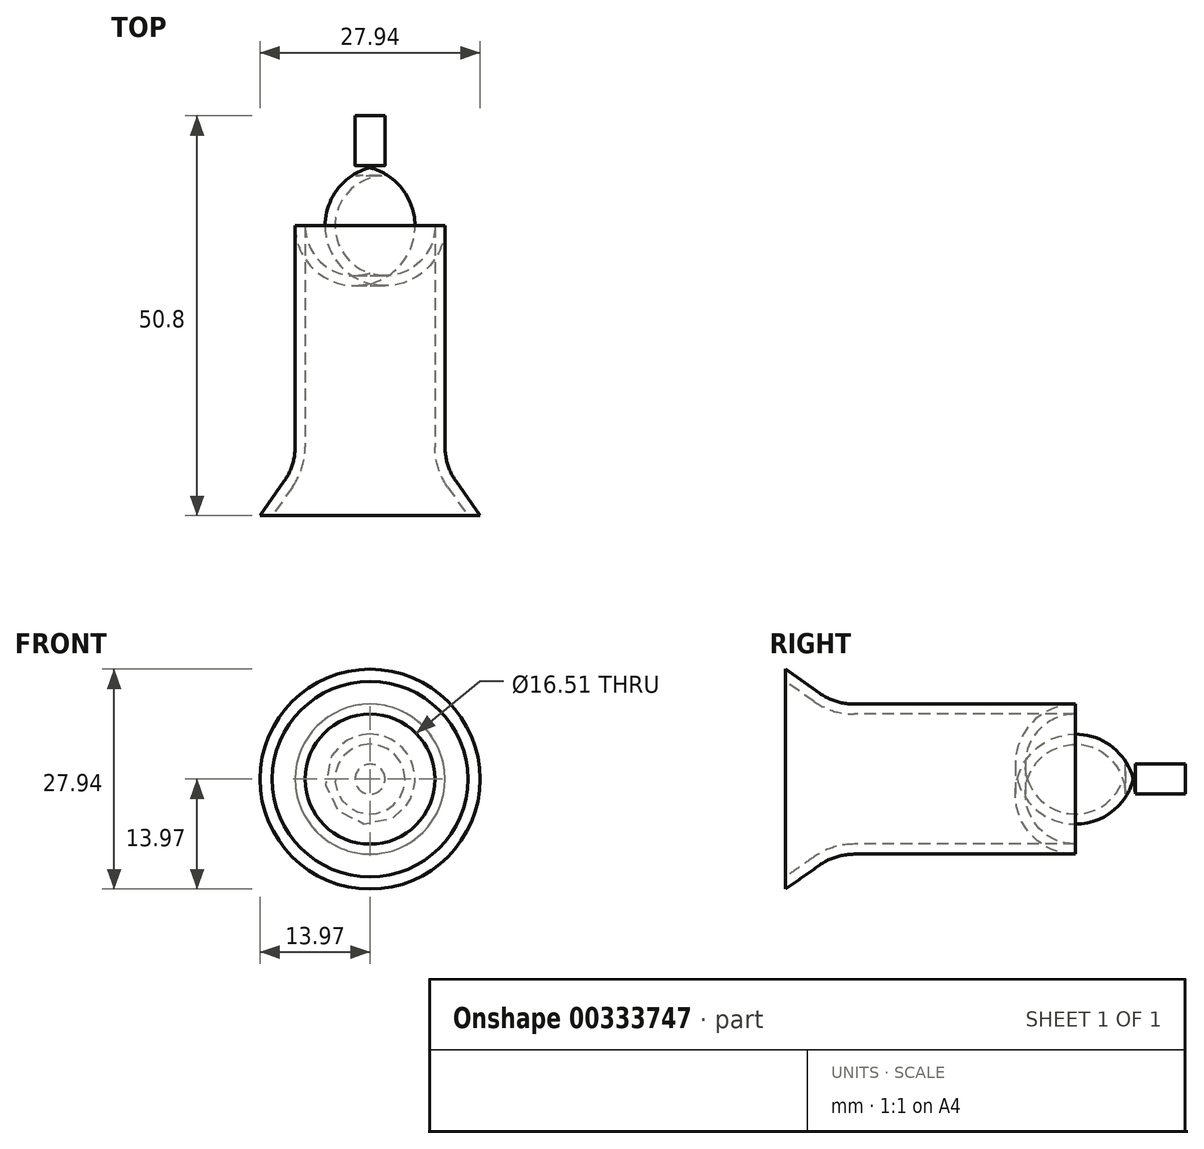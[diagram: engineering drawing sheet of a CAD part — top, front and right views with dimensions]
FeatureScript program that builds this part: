
annotation { "Feature Type Name" : "Feature", "Feature Type Description" : "" }
export const myFeature = defineFeature(function(context is Context, id is Id, definition is map)
    precondition{}
    {
        {
            var Q0;
            Q0=qCreatedBy(makeId("Front.planeOp"),FACE);
            var sketch = newSketch(context, id + "F0", { "sketchPlane" : qUnion([Q0])});
            skCircle(sketch, "E0", {"center": v(0, 0) * mm, "radius": 13.97 * mm});
            skSolve(sketch);
        }
        {
            var Q0;
            Q0=qCreatedBy(makeId("Front.planeOp"),FACE);
            cPlane(context, id + "F1", {"entities" : qUnion([Q0]), "cplaneType" : CPlaneType.OFFSET, "offset" : 6.35 * mm, "oppositeDirection" : true, "width" : 152.4 * mm, "height" : 152.4 * mm});
        }
        {
            var Q0;
            Q0=qCreatedBy(id+"F1.planeOp",FACE);
            var sketch = newSketch(context, id + "F2", { "sketchPlane" : qUnion([Q0])});
            skCircle(sketch, "E1", {"center": v(0, 0) * mm, "radius": 9.53 * mm});
            skSolve(sketch);
        }
        {
            var Q0;
            Q0=makeQuery(id+"F0.imprint","IMPRINT",FACE,{"disambiguationData":[TD([[makeQuery(id+"F0.imprint","IMPRINT",EDGE,{"derivedFrom":sQuery(id+"F0.wireOp",EDGE,"E0")}),1.0]])]});
            var Q1;
            Q1=makeQuery(id+"F2.imprint","IMPRINT",FACE,{"disambiguationData":[TD([[makeQuery(id+"F2.imprint","IMPRINT",EDGE,{"derivedFrom":sQuery(id+"F2.wireOp",EDGE,"E1")}),1.0]])]});
            loft(context, id + "F3", {"sheetProfilesArray" : [{ "sheetProfileEntities" : qUnion([Q0]) }, { "sheetProfileEntities" : qUnion([Q1]) }]});
        }
        {
            var Q0;
            Q0 = qSketchRegion(id + "F2", true);
            extrude(context, id + "F4", {"entities" : qUnion([Q0]), "operationType" : NewBodyOperationType.ADD, "oppositeDirection" : true, "depth" : 38.1 * mm});
        }
        {
            var Q0;
            {var subQ0=sQuery(id+"F2.wireOp",EDGE,"E1");Q0=makeQuery(id+"F4.boolean.opBoolean","MERGE",EDGE,{"derivedFrom":[makeQuery(id+"F3.opLoft","MID_CAP_EDGE",EDGE,{"disambiguationData":[OSD([sQuery(id+"F0.wireOp",EDGE,"E0"),subQ0])],"capPos":1.0}),makeQuery(id+"F4.opExtrude","CAP_EDGE",EDGE,{"disambiguationData":[OSD([subQ0])],"isStart":true})]});}
            fillet(context, id + "F5", {"entities" : qUnion([Q0]), "radius" : 7.62 * mm, "tangentPropagation" : true, "allowEdgeOverflow" : false});
        }
        {
            var Q0;
            Q0=makeQuery(id+"F4.opExtrude","CAP_EDGE",EDGE,{"disambiguationData":[OSD([sQuery(id+"F2.wireOp",EDGE,"E1")])],"isStart":false});
            fillet(context, id + "F6", {"entities" : qUnion([Q0]), "radius" : 7.62 * mm, "tangentPropagation" : true, "allowEdgeOverflow" : false});
        }
        {
            var Q0;
            Q0=makeQuery(id+"F4.opExtrude","CAP_FACE",FACE,{"disambiguationData":[OSD([sQuery(id+"F2.wireOp",EDGE,"E1")])],"isStart":false});
            extrude(context, id + "F7", {"entities" : qUnion([Q0]), "depth" : 6.35 * mm});
        }
        {
            var Q0;
            Q0=makeQuery(id+"F3.opLoft","CAP_FACE",FACE,{"disambiguationData":[OSD([makeQuery(id+"F0.imprint","IMPRINT",FACE,{"disambiguationData":[TD([[makeQuery(id+"F0.imprint","IMPRINT",EDGE,{"derivedFrom":sQuery(id+"F0.wireOp",EDGE,"E0")}),1.0]])]})])],"isStart":true});
            shell(context, id + "F8", {"entities" : qUnion([Q0]), "thickness" : 1.27 * mm});
        }
    });
